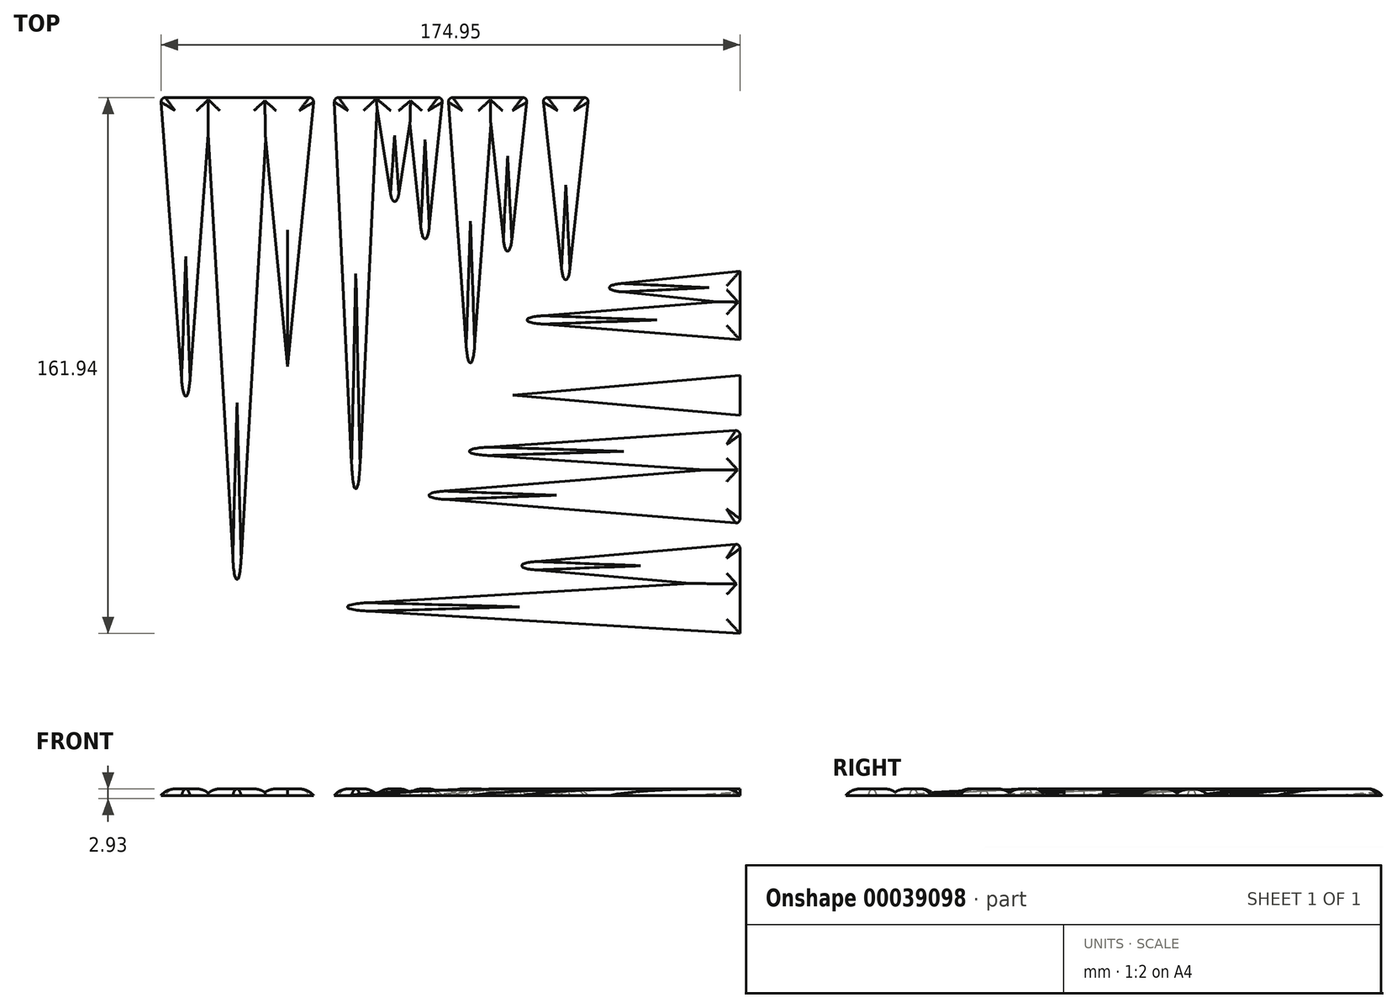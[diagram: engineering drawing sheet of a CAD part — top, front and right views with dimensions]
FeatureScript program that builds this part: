
annotation { "Feature Type Name" : "Feature", "Feature Type Description" : "" }
export const myFeature = defineFeature(function(context is Context, id is Id, definition is map)
    precondition{}
    {
        {
            var Q0;
            Q0=qCreatedBy(makeId("Top.planeOp"),FACE);
            var sketch = newSketch(context, id + "F0", { "sketchPlane" : qUnion([Q0])});
            skLineSegment(sketch, "E0.rect.bottom", {"start": v(-90, 90) * mm, "end": v(90, 90) * mm, "construction": true});
            skLineSegment(sketch, "E0.rect.top", {"start": v(-90, -90) * mm, "end": v(90, -90) * mm, "construction": true});
            skLineSegment(sketch, "E0.rect.left", {"start": v(-90, 90) * mm, "end": v(-90, -90) * mm, "construction": true});
            skLineSegment(sketch, "E0.rect.right", {"start": v(90, 90) * mm, "end": v(90, -90) * mm, "construction": true});
            skPoint(sketch, "E0.rect.middle", {"position": v(0, 0) * mm});
            skLineSegment(sketch, "E1", {"start": v(90, 90) * mm, "end": v(-90, -90) * mm, "construction": true});
            skLineSegment(sketch, "E2", {"start": v(25.7, 90) * mm, "end": v(19.75, 35.4) * mm});
            skLineSegment(sketch, "E3", {"start": v(19.75, 35.4) * mm, "end": v(13.8, 90) * mm});
            skLineSegment(sketch, "E4", {"start": v(15.26, 90) * mm, "end": v(8.54, -2.55) * mm});
            skLineSegment(sketch, "E5", {"start": v(8.54, -2.55) * mm, "end": v(1.8, 90) * mm});
            skLineSegment(sketch, "E6", {"start": v(1.8, 90) * mm, "end": v(0.16, 90) * mm});
            skLineSegment(sketch, "E7", {"start": v(0.16, 90) * mm, "end": v(-5.19, 38.8) * mm});
            skLineSegment(sketch, "E8", {"start": v(-5.19, 38.8) * mm, "end": v(-10.54, 90) * mm});
            skLineSegment(sketch, "E9", {"start": v(-8.5, 90) * mm, "end": v(-14.36, 53.07) * mm});
            skLineSegment(sketch, "E10", {"start": v(-14.36, 53.07) * mm, "end": v(-20.22, 90) * mm});
            skLineSegment(sketch, "E11", {"start": v(-19.57, 90) * mm, "end": v(-26.1, -47.23) * mm});
            skLineSegment(sketch, "E12", {"start": v(-26.1, -47.23) * mm, "end": v(-32.65, 90) * mm});
            skLineSegment(sketch, "E13", {"start": v(-85.05, 90) * mm, "end": v(-77.5, -12.44) * mm});
            skLineSegment(sketch, "E14", {"start": v(-77.5, -12.44) * mm, "end": v(-69.95, 90) * mm});
            skLineSegment(sketch, "E15", {"start": v(-71.42, 90) * mm, "end": v(-62.03, -71.1) * mm});
            skLineSegment(sketch, "E16", {"start": v(-62.03, -71.1) * mm, "end": v(-52.65, 90) * mm});
            skLineSegment(sketch, "E17", {"start": v(-54.62, 90) * mm, "end": v(-46.7, 8.72) * mm});
            skLineSegment(sketch, "E18", {"start": v(-46.7, 8.72) * mm, "end": v(-38.78, 90) * mm});
            skLineSegment(sketch, "E19", {"start": v(-85.05, 90) * mm, "end": v(-38.78, 90) * mm});
            skLineSegment(sketch, "E20", {"start": v(-32.65, 90) * mm, "end": v(0.16, 90) * mm});
            skLineSegment(sketch, "E21", {"start": v(1.8, 90) * mm, "end": v(25.7, 90) * mm});
            skLineSegment(sketch, "E22", {"start": v(30.42, 90) * mm, "end": v(37.34, 26.8) * mm});
            skLineSegment(sketch, "E23", {"start": v(37.34, 26.8) * mm, "end": v(44.27, 90) * mm});
            skLineSegment(sketch, "E24", {"start": v(44.27, 90) * mm, "end": v(30.42, 90) * mm});
            skLineSegment(sketch, "E25", {"start": v(90, -90) * mm, "end": v(90, -69.5) * mm});
            skLineSegment(sketch, "E26", {"start": v(90, -69.5) * mm, "end": v(-90, -79.75) * mm});
            skLineSegment(sketch, "E27", {"start": v(-90, -79.75) * mm, "end": v(90, -90) * mm});
            skLineSegment(sketch, "E28", {"start": v(90, -71.94) * mm, "end": v(-43.68, -63.95) * mm});
            skLineSegment(sketch, "E29", {"start": v(-43.68, -63.95) * mm, "end": v(90, -55.96) * mm});
            skLineSegment(sketch, "E30", {"start": v(90, -55.96) * mm, "end": v(90, -71.94) * mm});
            skLineSegment(sketch, "E31", {"start": v(90, -58.13) * mm, "end": v(13.75, -51.5) * mm});
            skLineSegment(sketch, "E32", {"start": v(13.75, -51.5) * mm, "end": v(90, -44.88) * mm});
            skLineSegment(sketch, "E33", {"start": v(90, -44.88) * mm, "end": v(90, -58.13) * mm});
            skLineSegment(sketch, "E34", {"start": v(90, -38.7) * mm, "end": v(-15.1, -30.22) * mm});
            skLineSegment(sketch, "E35", {"start": v(-15.1, -30.22) * mm, "end": v(90, -21.73) * mm});
            skLineSegment(sketch, "E36", {"start": v(90, -21.73) * mm, "end": v(90, -38.7) * mm});
            skLineSegment(sketch, "E37", {"start": v(90, -23.27) * mm, "end": v(-5.27, -16.92) * mm});
            skLineSegment(sketch, "E38", {"start": v(-5.27, -16.92) * mm, "end": v(90, -10.57) * mm});
            skLineSegment(sketch, "E39", {"start": v(90, -10.57) * mm, "end": v(90, -23.27) * mm});
            skLineSegment(sketch, "E40", {"start": v(90, 4.02) * mm, "end": v(11.13, 11.13) * mm});
            skLineSegment(sketch, "E41", {"start": v(11.13, 11.13) * mm, "end": v(90, 18.23) * mm});
            skLineSegment(sketch, "E42", {"start": v(90, 18.23) * mm, "end": v(90, 4.02) * mm});
            skLineSegment(sketch, "E43", {"start": v(90, 16.77) * mm, "end": v(14.4, 22.78) * mm});
            skLineSegment(sketch, "E44", {"start": v(14.4, 22.78) * mm, "end": v(90, 28.8) * mm});
            skLineSegment(sketch, "E45", {"start": v(90, 28.8) * mm, "end": v(90, 16.77) * mm});
            skLineSegment(sketch, "E46", {"start": v(90, 27.53) * mm, "end": v(42, 32.53) * mm});
            skLineSegment(sketch, "E47", {"start": v(42, 32.53) * mm, "end": v(90, 37.54) * mm});
            skLineSegment(sketch, "E48", {"start": v(90, 37.54) * mm, "end": v(90, 27.53) * mm});
            skLineSegment(sketch, "E49", {"start": v(90, -6) * mm, "end": v(21.32, 0) * mm});
            skLineSegment(sketch, "E50", {"start": v(21.32, 0) * mm, "end": v(90, 6) * mm});
            skLineSegment(sketch, "E51", {"start": v(90, 6) * mm, "end": v(90, -6) * mm});
            skSolve(sketch);
        }
        {
            var Q0;
            {var subQ3=sQuery(id+"F0.wireOp",EDGE,"E2");Q0=makeQuery(id+"F0.imprint","IMPRINT",FACE,{"disambiguationData":[TD([[makeQuery(id+"F0.imprint","IMPRINT",EDGE,{"derivedFrom":subQ3}),-1.0]])]});}
            var Q1;
            {var subQ1=sQuery(id+"F0.wireOp",EDGE,"E5");Q1=makeQuery(id+"F0.imprint","IMPRINT",FACE,{"disambiguationData":[TD([[makeQuery(id+"F0.imprint","IMPRINT",EDGE,{"derivedFrom":subQ1}),-1.0]])]});}
            var Q2;
            {var subQ5=sQuery(id+"F0.wireOp",EDGE,"E7");Q2=makeQuery(id+"F0.imprint","IMPRINT",FACE,{"disambiguationData":[TD([[makeQuery(id+"F0.imprint","IMPRINT",EDGE,{"derivedFrom":subQ5}),-1.0]])]});}
            var Q3;
            {var subQ1=sQuery(id+"F0.wireOp",EDGE,"E12");Q3=makeQuery(id+"F0.imprint","IMPRINT",FACE,{"disambiguationData":[TD([[makeQuery(id+"F0.imprint","IMPRINT",EDGE,{"derivedFrom":subQ1}),-1.0]])]});}
            var Q4;
            {var subQ3=sQuery(id+"F0.wireOp",EDGE,"E13");Q4=makeQuery(id+"F0.imprint","IMPRINT",FACE,{"disambiguationData":[TD([[makeQuery(id+"F0.imprint","IMPRINT",EDGE,{"derivedFrom":subQ3}),1.0]])]});}
            var Q5;
            {var subQ1=sQuery(id+"F0.wireOp",EDGE,"E18");Q5=makeQuery(id+"F0.imprint","IMPRINT",FACE,{"disambiguationData":[TD([[makeQuery(id+"F0.imprint","IMPRINT",EDGE,{"derivedFrom":subQ1}),1.0]])]});}
            var Q6;
            {var subQ0=sQuery(id+"F0.wireOp",EDGE,"E21");var subQ3=sQuery(id+"F0.wireOp",EDGE,"E3");var subQ4=makeQuery(id+"F0.imprint","INTERSECT",VERTEX,{"derivedFrom":[subQ3,subQ0]});Q6=makeQuery(id+"F0.imprint","IMPRINT",FACE,{"disambiguationData":[TD([[makeQuery(id+"F0.imprint","IMPRINT",EDGE,{"disambiguationData":[TD([[subQ4,1.0]])],"derivedFrom":subQ3}),-1.0]])]});}
            var Q7;
            {var subQ0=sQuery(id+"F0.wireOp",EDGE,"E20");var subQ3=sQuery(id+"F0.wireOp",EDGE,"E8");var subQ4=makeQuery(id+"F0.imprint","INTERSECT",VERTEX,{"derivedFrom":[subQ3,subQ0]});Q7=makeQuery(id+"F0.imprint","IMPRINT",FACE,{"disambiguationData":[TD([[makeQuery(id+"F0.imprint","IMPRINT",EDGE,{"disambiguationData":[TD([[subQ4,1.0]])],"derivedFrom":subQ3}),-1.0]])]});}
            var Q8;
            {var subQ0=sQuery(id+"F0.wireOp",EDGE,"E20");var subQ3=sQuery(id+"F0.wireOp",EDGE,"E8");var subQ4=makeQuery(id+"F0.imprint","INTERSECT",VERTEX,{"derivedFrom":[subQ3,subQ0]});Q8=makeQuery(id+"F0.imprint","IMPRINT",FACE,{"disambiguationData":[TD([[makeQuery(id+"F0.imprint","IMPRINT",EDGE,{"disambiguationData":[TD([[subQ4,1.0]])],"derivedFrom":subQ3}),1.0]])]});}
            var Q9;
            {var subQ0=sQuery(id+"F0.wireOp",EDGE,"E20");var subQ3=sQuery(id+"F0.wireOp",EDGE,"E10");var subQ4=makeQuery(id+"F0.imprint","INTERSECT",VERTEX,{"derivedFrom":[subQ3,subQ0]});Q9=makeQuery(id+"F0.imprint","IMPRINT",FACE,{"disambiguationData":[TD([[makeQuery(id+"F0.imprint","IMPRINT",EDGE,{"disambiguationData":[TD([[subQ4,1.0]])],"derivedFrom":subQ3}),-1.0]])]});}
            var Q10;
            {var subQ0=sQuery(id+"F0.wireOp",EDGE,"E19");var subQ3=sQuery(id+"F0.wireOp",EDGE,"E14");var subQ4=makeQuery(id+"F0.imprint","INTERSECT",VERTEX,{"derivedFrom":[subQ3,subQ0]});Q10=makeQuery(id+"F0.imprint","IMPRINT",FACE,{"disambiguationData":[TD([[makeQuery(id+"F0.imprint","IMPRINT",EDGE,{"disambiguationData":[TD([[subQ4,1.0]])],"derivedFrom":subQ3}),1.0]])]});}
            var Q11;
            {var subQ0=sQuery(id+"F0.wireOp",EDGE,"E14");var subQ3=sQuery(id+"F0.wireOp",EDGE,"E19");var subQ4=makeQuery(id+"F0.imprint","INTERSECT",VERTEX,{"derivedFrom":[subQ0,subQ3]});Q11=makeQuery(id+"F0.imprint","IMPRINT",FACE,{"disambiguationData":[TD([[makeQuery(id+"F0.imprint","IMPRINT",EDGE,{"disambiguationData":[TD([[subQ4,1.0]])],"derivedFrom":subQ0}),-1.0]])]});}
            var Q12;
            {var subQ0=sQuery(id+"F0.wireOp",EDGE,"E19");var subQ3=sQuery(id+"F0.wireOp",EDGE,"E16");var subQ4=makeQuery(id+"F0.imprint","INTERSECT",VERTEX,{"derivedFrom":[subQ3,subQ0]});Q12=makeQuery(id+"F0.imprint","IMPRINT",FACE,{"disambiguationData":[TD([[makeQuery(id+"F0.imprint","IMPRINT",EDGE,{"disambiguationData":[TD([[subQ4,1.0]])],"derivedFrom":subQ3}),1.0]])]});}
            var Q13;
            Q13=makeQuery(id+"F0.imprint","IMPRINT",FACE,{"disambiguationData":[TD([[makeQuery(id+"F0.imprint","IMPRINT",EDGE,{"derivedFrom":sQuery(id+"F0.wireOp",EDGE,"E22")}),1.0]])]});
            var Q14;
            {var subQ1=sQuery(id+"F0.wireOp",EDGE,"E47");Q14=makeQuery(id+"F0.imprint","IMPRINT",FACE,{"disambiguationData":[TD([[makeQuery(id+"F0.imprint","IMPRINT",EDGE,{"derivedFrom":subQ1}),-1.0]])]});}
            var Q15;
            {var subQ3=sQuery(id+"F0.wireOp",EDGE,"E45");var subQ6=sQuery(id+"F0.wireOp",EDGE,"E41");var subQ9=makeQuery(id+"F0.imprint","INTERSECT",VERTEX,{"derivedFrom":[subQ6,subQ3]});Q15=makeQuery(id+"F0.imprint","IMPRINT",FACE,{"disambiguationData":[TD([[makeQuery(id+"F0.imprint","IMPRINT",EDGE,{"disambiguationData":[TD([[subQ9,1.0]])],"derivedFrom":subQ6}),1.0]])]});}
            var Q16;
            {var subQ3=sQuery(id+"F0.wireOp",EDGE,"E42");Q16=makeQuery(id+"F0.imprint","IMPRINT",FACE,{"disambiguationData":[TD([[makeQuery(id+"F0.imprint","IMPRINT",EDGE,{"derivedFrom":subQ3}),-1.0]])]});}
            var Q17;
            {var subQ1=sQuery(id+"F0.wireOp",EDGE,"E49");Q17=makeQuery(id+"F0.imprint","IMPRINT",FACE,{"disambiguationData":[TD([[makeQuery(id+"F0.imprint","IMPRINT",EDGE,{"derivedFrom":subQ1}),-1.0]])]});}
            var Q18;
            {var subQ1=sQuery(id+"F0.wireOp",EDGE,"E38");Q18=makeQuery(id+"F0.imprint","IMPRINT",FACE,{"disambiguationData":[TD([[makeQuery(id+"F0.imprint","IMPRINT",EDGE,{"derivedFrom":subQ1}),-1.0]])]});}
            var Q19;
            {var subQ4=sQuery(id+"F0.wireOp",EDGE,"E34");Q19=makeQuery(id+"F0.imprint","IMPRINT",FACE,{"disambiguationData":[TD([[makeQuery(id+"F0.imprint","IMPRINT",EDGE,{"derivedFrom":subQ4}),-1.0]])]});}
            var Q20;
            {var subQ1=sQuery(id+"F0.wireOp",EDGE,"E32");Q20=makeQuery(id+"F0.imprint","IMPRINT",FACE,{"disambiguationData":[TD([[makeQuery(id+"F0.imprint","IMPRINT",EDGE,{"derivedFrom":subQ1}),-1.0]])]});}
            var Q21;
            {var subQ3=sQuery(id+"F0.wireOp",EDGE,"E30");var subQ5=sQuery(id+"F0.wireOp",EDGE,"E26");var subQ8=makeQuery(id+"F0.imprint","INTERSECT",VERTEX,{"derivedFrom":[subQ5,subQ3]});Q21=makeQuery(id+"F0.imprint","IMPRINT",FACE,{"disambiguationData":[TD([[makeQuery(id+"F0.imprint","IMPRINT",EDGE,{"disambiguationData":[TD([[subQ8,-1.0]])],"derivedFrom":subQ5}),-1.0]])]});}
            var Q22;
            {var subQ3=sQuery(id+"F0.wireOp",EDGE,"E25");Q22=makeQuery(id+"F0.imprint","IMPRINT",FACE,{"disambiguationData":[TD([[makeQuery(id+"F0.imprint","IMPRINT",EDGE,{"derivedFrom":subQ3}),1.0]])]});}
            var Q23;
            {var subQ0=sQuery(id+"F0.wireOp",EDGE,"E39");var subQ3=sQuery(id+"F0.wireOp",EDGE,"E35");var subQ4=makeQuery(id+"F0.imprint","INTERSECT",VERTEX,{"derivedFrom":[subQ3,subQ0]});Q23=makeQuery(id+"F0.imprint","IMPRINT",FACE,{"disambiguationData":[TD([[makeQuery(id+"F0.imprint","IMPRINT",EDGE,{"disambiguationData":[TD([[subQ4,1.0]])],"derivedFrom":subQ3}),-1.0]])]});}
            var Q24;
            {var subQ0=sQuery(id+"F0.wireOp",EDGE,"E33");var subQ3=sQuery(id+"F0.wireOp",EDGE,"E29");var subQ4=makeQuery(id+"F0.imprint","INTERSECT",VERTEX,{"derivedFrom":[subQ3,subQ0]});Q24=makeQuery(id+"F0.imprint","IMPRINT",FACE,{"disambiguationData":[TD([[makeQuery(id+"F0.imprint","IMPRINT",EDGE,{"disambiguationData":[TD([[subQ4,1.0]])],"derivedFrom":subQ3}),-1.0]])]});}
            var Q25;
            {var subQ0=sQuery(id+"F0.wireOp",EDGE,"E51");var subQ3=sQuery(id+"F0.wireOp",EDGE,"E40");var subQ4=makeQuery(id+"F0.imprint","INTERSECT",VERTEX,{"derivedFrom":[subQ3,subQ0]});Q25=makeQuery(id+"F0.imprint","IMPRINT",FACE,{"disambiguationData":[TD([[makeQuery(id+"F0.imprint","IMPRINT",EDGE,{"disambiguationData":[TD([[subQ4,-1.0]])],"derivedFrom":subQ3}),-1.0]])]});}
            var Q26;
            {var subQ0=sQuery(id+"F0.wireOp",EDGE,"E48");var subQ3=sQuery(id+"F0.wireOp",EDGE,"E44");var subQ4=makeQuery(id+"F0.imprint","INTERSECT",VERTEX,{"derivedFrom":[subQ3,subQ0]});Q26=makeQuery(id+"F0.imprint","IMPRINT",FACE,{"disambiguationData":[TD([[makeQuery(id+"F0.imprint","IMPRINT",EDGE,{"disambiguationData":[TD([[subQ4,1.0]])],"derivedFrom":subQ3}),-1.0]])]});}
            var Q27;
            {var subQ0=sQuery(id+"F0.wireOp",EDGE,"E30");var subQ1=sQuery(id+"F0.wireOp",EDGE,"E26");var subQ2=makeQuery(id+"F0.imprint","INTERSECT",VERTEX,{"derivedFrom":[subQ1,subQ0]});Q27=makeQuery(id+"F0.imprint","IMPRINT",FACE,{"disambiguationData":[TD([[makeQuery(id+"F0.imprint","IMPRINT",EDGE,{"disambiguationData":[TD([[subQ2,-1.0]])],"derivedFrom":subQ1}),1.0]])]});}
            var Q28;
            {var subQ0=sQuery(id+"F0.wireOp",EDGE,"E45");var subQ3=sQuery(id+"F0.wireOp",EDGE,"E41");var subQ4=makeQuery(id+"F0.imprint","INTERSECT",VERTEX,{"derivedFrom":[subQ3,subQ0]});Q28=makeQuery(id+"F0.imprint","IMPRINT",FACE,{"disambiguationData":[TD([[makeQuery(id+"F0.imprint","IMPRINT",EDGE,{"disambiguationData":[TD([[subQ4,1.0]])],"derivedFrom":subQ3}),-1.0]])]});}
            extrude(context, id + "F1", {"entities" : qUnion([Q0, Q1, Q2, Q3, Q4, Q5, Q6, Q7, Q8, Q9, Q10, Q11, Q12, Q13, Q14, Q15, Q16, Q17, Q18, Q19, Q20, Q21, Q22, Q23, Q24, Q25, Q26, Q27, Q28]), "depth" : 2 * mm});
        }
        {
            var Q0;
            Q0=makeQuery(id+"F1.opExtrude","CAP_FACE",FACE,{"disambiguationData":[OSD([sQuery(id+"F0.wireOp",EDGE,"E13"),sQuery(id+"F0.wireOp",EDGE,"E14"),sQuery(id+"F0.wireOp",EDGE,"E19")])],"isStart":false});
            var Q1;
            Q1=makeQuery(id+"F1.opExtrude","CAP_FACE",FACE,{"disambiguationData":[OSD([sQuery(id+"F0.wireOp",EDGE,"E15"),sQuery(id+"F0.wireOp",EDGE,"E16"),sQuery(id+"F0.wireOp",EDGE,"E19")])],"isStart":false});
            var Q2;
            Q2=makeQuery(id+"F1.opExtrude","CAP_FACE",FACE,{"disambiguationData":[OSD([sQuery(id+"F0.wireOp",EDGE,"E17"),sQuery(id+"F0.wireOp",EDGE,"E18"),sQuery(id+"F0.wireOp",EDGE,"E19")])],"isStart":false});
            var Q3;
            Q3=makeQuery(id+"F1.opExtrude","CAP_FACE",FACE,{"disambiguationData":[OSD([sQuery(id+"F0.wireOp",EDGE,"E11"),sQuery(id+"F0.wireOp",EDGE,"E12"),sQuery(id+"F0.wireOp",EDGE,"E20")])],"isStart":false});
            var Q4;
            Q4=makeQuery(id+"F1.opExtrude","CAP_FACE",FACE,{"disambiguationData":[OSD([sQuery(id+"F0.wireOp",EDGE,"E9"),sQuery(id+"F0.wireOp",EDGE,"E10"),sQuery(id+"F0.wireOp",EDGE,"E20")])],"isStart":false});
            var Q5;
            Q5=makeQuery(id+"F1.opExtrude","CAP_FACE",FACE,{"disambiguationData":[OSD([sQuery(id+"F0.wireOp",EDGE,"E7"),sQuery(id+"F0.wireOp",EDGE,"E8"),sQuery(id+"F0.wireOp",EDGE,"E20")])],"isStart":false});
            var Q6;
            Q6=makeQuery(id+"F1.opExtrude","CAP_FACE",FACE,{"disambiguationData":[OSD([sQuery(id+"F0.wireOp",EDGE,"E4"),sQuery(id+"F0.wireOp",EDGE,"E5"),sQuery(id+"F0.wireOp",EDGE,"E21")])],"isStart":false});
            var Q7;
            Q7=makeQuery(id+"F1.opExtrude","CAP_FACE",FACE,{"disambiguationData":[OSD([sQuery(id+"F0.wireOp",EDGE,"E2"),sQuery(id+"F0.wireOp",EDGE,"E3"),sQuery(id+"F0.wireOp",EDGE,"E21")])],"isStart":false});
            var Q8;
            Q8=makeQuery(id+"F1.opExtrude","CAP_FACE",FACE,{"disambiguationData":[OSD([sQuery(id+"F0.wireOp",EDGE,"E22"),sQuery(id+"F0.wireOp",EDGE,"E23"),sQuery(id+"F0.wireOp",EDGE,"E24")])],"isStart":false});
            var Q9;
            Q9=makeQuery(id+"F1.opExtrude","CAP_FACE",FACE,{"disambiguationData":[OSD([sQuery(id+"F0.wireOp",EDGE,"E40"),sQuery(id+"F0.wireOp",EDGE,"E41"),sQuery(id+"F0.wireOp",EDGE,"E42"),sQuery(id+"F0.wireOp",EDGE,"E43"),sQuery(id+"F0.wireOp",EDGE,"E44"),sQuery(id+"F0.wireOp",EDGE,"E45"),sQuery(id+"F0.wireOp",EDGE,"E46"),sQuery(id+"F0.wireOp",EDGE,"E47"),sQuery(id+"F0.wireOp",EDGE,"E48"),sQuery(id+"F0.wireOp",EDGE,"E49"),sQuery(id+"F0.wireOp",EDGE,"E50"),sQuery(id+"F0.wireOp",EDGE,"E51")])],"isStart":false});
            var Q10;
            Q10=makeQuery(id+"F1.opExtrude","CAP_FACE",FACE,{"disambiguationData":[OSD([sQuery(id+"F0.wireOp",EDGE,"E34"),sQuery(id+"F0.wireOp",EDGE,"E35"),sQuery(id+"F0.wireOp",EDGE,"E36"),sQuery(id+"F0.wireOp",EDGE,"E37"),sQuery(id+"F0.wireOp",EDGE,"E38"),sQuery(id+"F0.wireOp",EDGE,"E39")])],"isStart":false});
            var Q11;
            Q11=makeQuery(id+"F1.opExtrude","CAP_FACE",FACE,{"disambiguationData":[OSD([sQuery(id+"F0.wireOp",EDGE,"E25"),sQuery(id+"F0.wireOp",EDGE,"E26"),sQuery(id+"F0.wireOp",EDGE,"E27"),sQuery(id+"F0.wireOp",EDGE,"E28"),sQuery(id+"F0.wireOp",EDGE,"E29"),sQuery(id+"F0.wireOp",EDGE,"E30"),sQuery(id+"F0.wireOp",EDGE,"E31"),sQuery(id+"F0.wireOp",EDGE,"E32"),sQuery(id+"F0.wireOp",EDGE,"E33")])],"isStart":false});
            fillet(context, id + "F2", {"entities" : qUnion([Q0, Q1, Q2, Q3, Q4, Q5, Q6, Q7, Q8, Q9, Q10, Q11]), "radius" : 5 * mm, "tangentPropagation" : true, "allowEdgeOverflow" : false});
        }
        {
            var Q0;
            Q0=makeQuery(id+"F2.opFillet","BLEND_EDGE",EDGE,{"blendedFrom":[makeQuery(id+"F1.opExtrude","CAP_EDGE",EDGE,{"disambiguationData":[OSD([sQuery(id+"F0.wireOp",EDGE,"E13")])],"isStart":false}),makeQuery(id+"F1.opExtrude","CAP_EDGE",EDGE,{"disambiguationData":[OSD([sQuery(id+"F0.wireOp",EDGE,"E19")])],"isStart":false})],"blendedInto":[]});
            var Q1;
            Q1=makeQuery(id+"F2.opFillet","BLEND_EDGE",EDGE,{"blendedFrom":[makeQuery(id+"F1.opExtrude","CAP_EDGE",EDGE,{"disambiguationData":[OSD([sQuery(id+"F0.wireOp",EDGE,"E13")])],"isStart":false}),makeQuery(id+"F1.opExtrude","CAP_EDGE",EDGE,{"disambiguationData":[OSD([sQuery(id+"F0.wireOp",EDGE,"E14")])],"isStart":false})],"blendedInto":[]});
            var Q2;
            Q2=makeQuery(id+"F2.opFillet","BLEND_EDGE",EDGE,{"blendedFrom":[makeQuery(id+"F1.opExtrude","CAP_EDGE",EDGE,{"disambiguationData":[OSD([sQuery(id+"F0.wireOp",EDGE,"E18")])],"isStart":false}),makeQuery(id+"F1.opExtrude","CAP_EDGE",EDGE,{"disambiguationData":[OSD([sQuery(id+"F0.wireOp",EDGE,"E19")])],"isStart":false})],"blendedInto":[]});
            var Q3;
            Q3=makeQuery(id+"F2.opFillet","BLEND_EDGE",EDGE,{"blendedFrom":[makeQuery(id+"F1.opExtrude","CAP_EDGE",EDGE,{"disambiguationData":[OSD([sQuery(id+"F0.wireOp",EDGE,"E15")])],"isStart":false}),makeQuery(id+"F1.opExtrude","CAP_EDGE",EDGE,{"disambiguationData":[OSD([sQuery(id+"F0.wireOp",EDGE,"E16")])],"isStart":false})],"blendedInto":[]});
            var Q4;
            Q4=makeQuery(id+"F2.opFillet","BLEND_EDGE",EDGE,{"blendedFrom":[makeQuery(id+"F1.opExtrude","CAP_EDGE",EDGE,{"disambiguationData":[OSD([sQuery(id+"F0.wireOp",EDGE,"E11")])],"isStart":false}),makeQuery(id+"F1.opExtrude","CAP_EDGE",EDGE,{"disambiguationData":[OSD([sQuery(id+"F0.wireOp",EDGE,"E12")])],"isStart":false})],"blendedInto":[]});
            var Q5;
            Q5=makeQuery(id+"F2.opFillet","BLEND_EDGE",EDGE,{"blendedFrom":[makeQuery(id+"F1.opExtrude","CAP_EDGE",EDGE,{"disambiguationData":[OSD([sQuery(id+"F0.wireOp",EDGE,"E9")])],"isStart":false}),makeQuery(id+"F1.opExtrude","CAP_EDGE",EDGE,{"disambiguationData":[OSD([sQuery(id+"F0.wireOp",EDGE,"E10")])],"isStart":false})],"blendedInto":[]});
            var Q6;
            Q6=makeQuery(id+"F2.opFillet","BLEND_EDGE",EDGE,{"blendedFrom":[makeQuery(id+"F1.opExtrude","CAP_EDGE",EDGE,{"disambiguationData":[OSD([sQuery(id+"F0.wireOp",EDGE,"E7")])],"isStart":false}),makeQuery(id+"F1.opExtrude","CAP_EDGE",EDGE,{"disambiguationData":[OSD([sQuery(id+"F0.wireOp",EDGE,"E8")])],"isStart":false})],"blendedInto":[]});
            var Q7;
            Q7=makeQuery(id+"F2.opFillet","BLEND_EDGE",EDGE,{"blendedFrom":[makeQuery(id+"F1.opExtrude","CAP_EDGE",EDGE,{"disambiguationData":[OSD([sQuery(id+"F0.wireOp",EDGE,"E4")])],"isStart":false}),makeQuery(id+"F1.opExtrude","CAP_EDGE",EDGE,{"disambiguationData":[OSD([sQuery(id+"F0.wireOp",EDGE,"E5")])],"isStart":false})],"blendedInto":[]});
            var Q8;
            Q8=makeQuery(id+"F2.opFillet","BLEND_EDGE",EDGE,{"blendedFrom":[makeQuery(id+"F1.opExtrude","CAP_EDGE",EDGE,{"disambiguationData":[OSD([sQuery(id+"F0.wireOp",EDGE,"E2")])],"isStart":false}),makeQuery(id+"F1.opExtrude","CAP_EDGE",EDGE,{"disambiguationData":[OSD([sQuery(id+"F0.wireOp",EDGE,"E3")])],"isStart":false})],"blendedInto":[]});
            var Q9;
            Q9=makeQuery(id+"F2.opFillet","BLEND_EDGE",EDGE,{"blendedFrom":[makeQuery(id+"F1.opExtrude","CAP_EDGE",EDGE,{"disambiguationData":[OSD([sQuery(id+"F0.wireOp",EDGE,"E22")])],"isStart":false}),makeQuery(id+"F1.opExtrude","CAP_EDGE",EDGE,{"disambiguationData":[OSD([sQuery(id+"F0.wireOp",EDGE,"E23")])],"isStart":false})],"blendedInto":[]});
            var Q10;
            Q10=makeQuery(id+"F2.opFillet","BLEND_EDGE",EDGE,{"blendedFrom":[makeQuery(id+"F1.opExtrude","CAP_EDGE",EDGE,{"disambiguationData":[OSD([sQuery(id+"F0.wireOp",EDGE,"E23")])],"isStart":false}),makeQuery(id+"F1.opExtrude","CAP_EDGE",EDGE,{"disambiguationData":[OSD([sQuery(id+"F0.wireOp",EDGE,"E24")])],"isStart":false})],"blendedInto":[]});
            var Q11;
            Q11=makeQuery(id+"F2.opFillet","BLEND_EDGE",EDGE,{"blendedFrom":[makeQuery(id+"F1.opExtrude","CAP_EDGE",EDGE,{"disambiguationData":[OSD([sQuery(id+"F0.wireOp",EDGE,"E22")])],"isStart":false}),makeQuery(id+"F1.opExtrude","CAP_EDGE",EDGE,{"disambiguationData":[OSD([sQuery(id+"F0.wireOp",EDGE,"E24")])],"isStart":false})],"blendedInto":[]});
            var Q12;
            Q12=makeQuery(id+"F2.opFillet","BLEND_EDGE",EDGE,{"blendedFrom":[makeQuery(id+"F1.opExtrude","CAP_EDGE",EDGE,{"disambiguationData":[OSD([sQuery(id+"F0.wireOp",EDGE,"E2")])],"isStart":false}),makeQuery(id+"F1.opExtrude","CAP_EDGE",EDGE,{"disambiguationData":[OSD([sQuery(id+"F0.wireOp",EDGE,"E21")])],"isStart":false})],"blendedInto":[]});
            var Q13;
            Q13=makeQuery(id+"F2.opFillet","BLEND_EDGE",EDGE,{"blendedFrom":[makeQuery(id+"F1.opExtrude","CAP_EDGE",EDGE,{"disambiguationData":[OSD([sQuery(id+"F0.wireOp",EDGE,"E5")])],"isStart":false}),makeQuery(id+"F1.opExtrude","CAP_EDGE",EDGE,{"disambiguationData":[OSD([sQuery(id+"F0.wireOp",EDGE,"E21")])],"isStart":false})],"blendedInto":[]});
            var Q14;
            Q14=makeQuery(id+"F2.opFillet","BLEND_EDGE",EDGE,{"blendedFrom":[makeQuery(id+"F1.opExtrude","CAP_EDGE",EDGE,{"disambiguationData":[OSD([sQuery(id+"F0.wireOp",EDGE,"E7")])],"isStart":false}),makeQuery(id+"F1.opExtrude","CAP_EDGE",EDGE,{"disambiguationData":[OSD([sQuery(id+"F0.wireOp",EDGE,"E20")])],"isStart":false})],"blendedInto":[]});
            var Q15;
            Q15=makeQuery(id+"F2.opFillet","BLEND_EDGE",EDGE,{"blendedFrom":[makeQuery(id+"F1.opExtrude","CAP_EDGE",EDGE,{"disambiguationData":[OSD([sQuery(id+"F0.wireOp",EDGE,"E12")])],"isStart":false}),makeQuery(id+"F1.opExtrude","CAP_EDGE",EDGE,{"disambiguationData":[OSD([sQuery(id+"F0.wireOp",EDGE,"E20")])],"isStart":false})],"blendedInto":[]});
            var Q16;
            Q16=makeQuery(id+"F2.opFillet","BLEND_EDGE",EDGE,{"blendedFrom":[makeQuery(id+"F1.opExtrude","CAP_EDGE",EDGE,{"disambiguationData":[OSD([sQuery(id+"F0.wireOp",EDGE,"E46")])],"isStart":false}),makeQuery(id+"F1.opExtrude","CAP_EDGE",EDGE,{"disambiguationData":[OSD([sQuery(id+"F0.wireOp",EDGE,"E47")])],"isStart":false})],"blendedInto":[]});
            var Q17;
            Q17=makeQuery(id+"F2.opFillet","BLEND_EDGE",EDGE,{"blendedFrom":[makeQuery(id+"F1.opExtrude","CAP_EDGE",EDGE,{"disambiguationData":[OSD([sQuery(id+"F0.wireOp",EDGE,"E43")])],"isStart":false}),makeQuery(id+"F1.opExtrude","CAP_EDGE",EDGE,{"disambiguationData":[OSD([sQuery(id+"F0.wireOp",EDGE,"E44")])],"isStart":false})],"blendedInto":[]});
            var Q18;
            Q18=makeQuery(id+"F2.opFillet","BLEND_EDGE",EDGE,{"blendedFrom":[makeQuery(id+"F1.opExtrude","CAP_EDGE",EDGE,{"disambiguationData":[OSD([sQuery(id+"F0.wireOp",EDGE,"E40")])],"isStart":false}),makeQuery(id+"F1.opExtrude","CAP_EDGE",EDGE,{"disambiguationData":[OSD([sQuery(id+"F0.wireOp",EDGE,"E41")])],"isStart":false})],"blendedInto":[]});
            var Q19;
            Q19=makeQuery(id+"F2.opFillet","BLEND_EDGE",EDGE,{"blendedFrom":[makeQuery(id+"F1.opExtrude","CAP_EDGE",EDGE,{"disambiguationData":[OSD([sQuery(id+"F0.wireOp",EDGE,"E49")])],"isStart":false}),makeQuery(id+"F1.opExtrude","CAP_EDGE",EDGE,{"disambiguationData":[OSD([sQuery(id+"F0.wireOp",EDGE,"E50")])],"isStart":false})],"blendedInto":[]});
            var Q20;
            Q20=makeQuery(id+"F2.opFillet","BLEND_EDGE",EDGE,{"blendedFrom":[makeQuery(id+"F1.opExtrude","CAP_EDGE",EDGE,{"disambiguationData":[OSD([sQuery(id+"F0.wireOp",EDGE,"E37")])],"isStart":false}),makeQuery(id+"F1.opExtrude","CAP_EDGE",EDGE,{"disambiguationData":[OSD([sQuery(id+"F0.wireOp",EDGE,"E38")])],"isStart":false})],"blendedInto":[]});
            var Q21;
            Q21=makeQuery(id+"F2.opFillet","BLEND_EDGE",EDGE,{"blendedFrom":[makeQuery(id+"F1.opExtrude","CAP_EDGE",EDGE,{"disambiguationData":[OSD([sQuery(id+"F0.wireOp",EDGE,"E34")])],"isStart":false}),makeQuery(id+"F1.opExtrude","CAP_EDGE",EDGE,{"disambiguationData":[OSD([sQuery(id+"F0.wireOp",EDGE,"E35")])],"isStart":false})],"blendedInto":[]});
            var Q22;
            Q22=makeQuery(id+"F2.opFillet","BLEND_EDGE",EDGE,{"blendedFrom":[makeQuery(id+"F1.opExtrude","CAP_EDGE",EDGE,{"disambiguationData":[OSD([sQuery(id+"F0.wireOp",EDGE,"E31")])],"isStart":false}),makeQuery(id+"F1.opExtrude","CAP_EDGE",EDGE,{"disambiguationData":[OSD([sQuery(id+"F0.wireOp",EDGE,"E32")])],"isStart":false})],"blendedInto":[]});
            var Q23;
            Q23=makeQuery(id+"F2.opFillet","BLEND_EDGE",EDGE,{"blendedFrom":[makeQuery(id+"F1.opExtrude","CAP_EDGE",EDGE,{"disambiguationData":[OSD([sQuery(id+"F0.wireOp",EDGE,"E28")])],"isStart":false}),makeQuery(id+"F1.opExtrude","CAP_EDGE",EDGE,{"disambiguationData":[OSD([sQuery(id+"F0.wireOp",EDGE,"E29")])],"isStart":false})],"blendedInto":[]});
            var Q24;
            Q24=makeQuery(id+"F2.opFillet","BLEND_EDGE",EDGE,{"blendedFrom":[makeQuery(id+"F1.opExtrude","CAP_EDGE",EDGE,{"disambiguationData":[OSD([sQuery(id+"F0.wireOp",EDGE,"E26")])],"isStart":false}),makeQuery(id+"F1.opExtrude","CAP_EDGE",EDGE,{"disambiguationData":[OSD([sQuery(id+"F0.wireOp",EDGE,"E27")])],"isStart":false})],"blendedInto":[]});
            var Q25;
            Q25=makeQuery(id+"F2.opFillet","BLEND_EDGE",EDGE,{"blendedFrom":[makeQuery(id+"F1.opExtrude","CAP_EDGE",EDGE,{"disambiguationData":[OSD([sQuery(id+"F0.wireOp",EDGE,"E25"),sQuery(id+"F0.wireOp",EDGE,"E30"),sQuery(id+"F0.wireOp",EDGE,"E33")])],"isStart":false}),makeQuery(id+"F1.opExtrude","CAP_EDGE",EDGE,{"disambiguationData":[OSD([sQuery(id+"F0.wireOp",EDGE,"E27")])],"isStart":false})],"blendedInto":[]});
            var Q26;
            Q26=makeQuery(id+"F2.opFillet","BLEND_EDGE",EDGE,{"blendedFrom":[makeQuery(id+"F1.opExtrude","CAP_EDGE",EDGE,{"disambiguationData":[OSD([sQuery(id+"F0.wireOp",EDGE,"E25"),sQuery(id+"F0.wireOp",EDGE,"E30"),sQuery(id+"F0.wireOp",EDGE,"E33")])],"isStart":false}),makeQuery(id+"F1.opExtrude","CAP_EDGE",EDGE,{"disambiguationData":[OSD([sQuery(id+"F0.wireOp",EDGE,"E32")])],"isStart":false})],"blendedInto":[]});
            var Q27;
            Q27=makeQuery(id+"F2.opFillet","BLEND_EDGE",EDGE,{"blendedFrom":[makeQuery(id+"F1.opExtrude","CAP_EDGE",EDGE,{"disambiguationData":[OSD([sQuery(id+"F0.wireOp",EDGE,"E34")])],"isStart":false}),makeQuery(id+"F1.opExtrude","CAP_EDGE",EDGE,{"disambiguationData":[OSD([sQuery(id+"F0.wireOp",EDGE,"E36"),sQuery(id+"F0.wireOp",EDGE,"E39")])],"isStart":false})],"blendedInto":[]});
            var Q28;
            Q28=makeQuery(id+"F2.opFillet","BLEND_EDGE",EDGE,{"blendedFrom":[makeQuery(id+"F1.opExtrude","CAP_EDGE",EDGE,{"disambiguationData":[OSD([sQuery(id+"F0.wireOp",EDGE,"E36"),sQuery(id+"F0.wireOp",EDGE,"E39")])],"isStart":false}),makeQuery(id+"F1.opExtrude","CAP_EDGE",EDGE,{"disambiguationData":[OSD([sQuery(id+"F0.wireOp",EDGE,"E38")])],"isStart":false})],"blendedInto":[]});
            fillet(context, id + "F3", {"entities" : qUnion([Q0, Q1, Q2, Q3, Q4, Q5, Q6, Q7, Q8, Q9, Q10, Q11, Q12, Q13, Q14, Q15, Q16, Q17, Q18, Q19, Q20, Q21, Q22, Q23, Q24, Q25, Q26, Q27, Q28]), "radius" : 1.6 * mm, "tangentPropagation" : true, "allowEdgeOverflow" : false});
        }
    });
